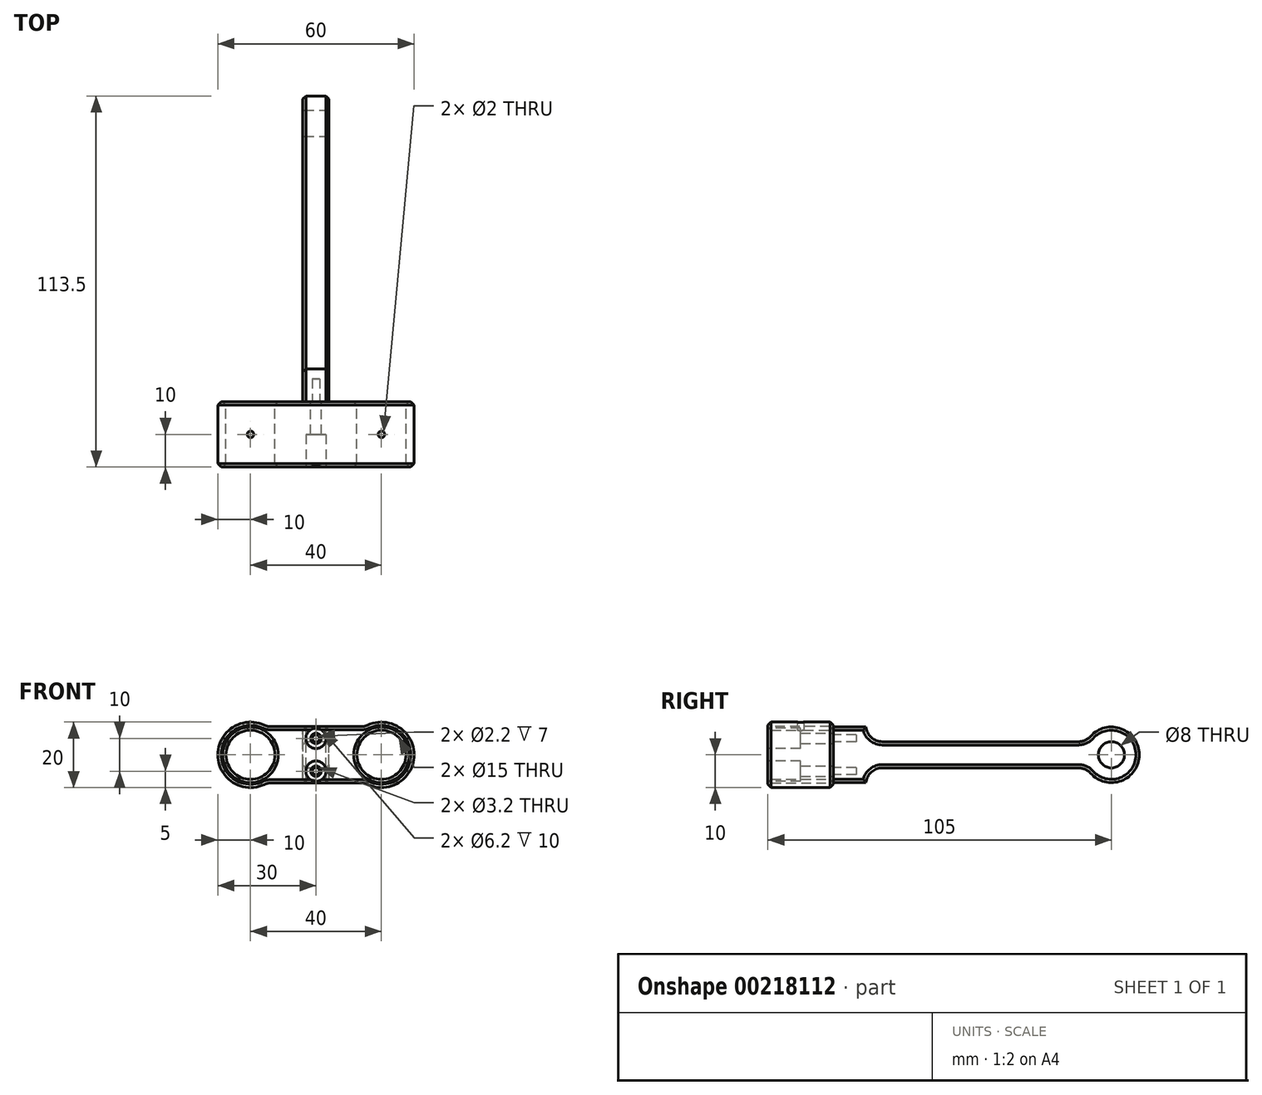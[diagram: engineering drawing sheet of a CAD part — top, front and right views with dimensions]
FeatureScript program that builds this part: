
annotation { "Feature Type Name" : "Feature", "Feature Type Description" : "" }
export const myFeature = defineFeature(function(context is Context, id is Id, definition is map)
    precondition{}
    {
        {
            var Q0;
            Q0=qCreatedBy(makeId("Front.planeOp"),FACE);
            var sketch = newSketch(context, id + "F0", { "sketchPlane" : qUnion([Q0])});
            skPoint(sketch, "E0.middle", {"position": v(0, 0) * mm});
            skCircle(sketch, "E1", {"center": v(-20, 0) * mm, "radius": 7.5 * mm});
            skCircle(sketch, "E2", {"center": v(20, 0) * mm, "radius": 7.5 * mm});
            skCircle(sketch, "E3", {"center": v(0, 5) * mm, "radius": 1.6 * mm});
            skCircle(sketch, "E4", {"center": v(0, -5) * mm, "radius": 1.6 * mm});
            skArc(sketch, "E5", {"start": v(-14.89, 8.6) * mm, "mid": v(-30, 0) * mm, "end": v(-14.89, -8.6) * mm});
            skArc(sketch, "E6", {"start": v(14.89, -8.6) * mm, "mid": v(30, 0) * mm, "end": v(14.89, 8.6) * mm});
            skLineSegment(sketch, "E7.bottom", {"start": v(14.89, 8.6) * mm, "end": v(-14.89, 8.6) * mm});
            skLineSegment(sketch, "E7.top", {"start": v(14.89, -8.6) * mm, "end": v(-14.89, -8.6) * mm});
            skPoint(sketch, "E8.orphan", {"position": v(30, 10) * mm});
            skPoint(sketch, "E9.orphan", {"position": v(-30, 10) * mm});
            skPoint(sketch, "E10.orphan", {"position": v(-30, -10) * mm});
            skPoint(sketch, "E0.left.start.orphan", {"position": v(30, -10) * mm});
            skSolve(sketch);
        }
        {
            var Q0;
            Q0=makeQuery(id+"F0.imprint","IMPRINT",FACE,{"disambiguationData":[TD([[makeQuery(id+"F0.imprint","IMPRINT",EDGE,{"derivedFrom":sQuery(id+"F0.wireOp",EDGE,"E0.bottom")}),-1.0]])]});
            var Q1;
            Q1=makeQuery(id+"F0.imprint","IMPRINT",FACE,{"disambiguationData":[TD([[makeQuery(id+"F0.imprint","IMPRINT",EDGE,{"derivedFrom":sQuery(id+"F0.wireOp",EDGE,"E1")}),-1.0]])]});
            extrude(context, id + "F1", {"entities" : qUnion([Q0, Q1]), "depth" : 20 * mm});
        }
        {
            var Q0;
            Q0=makeQuery(id+"F1.opExtrude","CAP_FACE",FACE,{"disambiguationData":[OSD([sQuery(id+"F0.wireOp",EDGE,"E0.bottom"),sQuery(id+"F0.wireOp",EDGE,"E0.top"),sQuery(id+"F0.wireOp",EDGE,"E0.left"),sQuery(id+"F0.wireOp",EDGE,"E0.right"),sQuery(id+"F0.wireOp",EDGE,"E1"),sQuery(id+"F0.wireOp",EDGE,"E2"),sQuery(id+"F0.wireOp",EDGE,"E3"),sQuery(id+"F0.wireOp",EDGE,"E4")])],"isStart":true});
            var sketch = newSketch(context, id + "F2", { "sketchPlane" : qUnion([Q0])});
            skLineSegment(sketch, "E11.bottom", {"start": v(4, -8.5) * mm, "end": v(-4, -8.5) * mm});
            skLineSegment(sketch, "E11.top", {"start": v(4, 8.5) * mm, "end": v(-4, 8.5) * mm});
            skLineSegment(sketch, "E11.left", {"start": v(4, -8.5) * mm, "end": v(4, 8.5) * mm});
            skLineSegment(sketch, "E11.right", {"start": v(-4, -8.5) * mm, "end": v(-4, 8.5) * mm});
            skPoint(sketch, "E11.middle", {"position": v(0, 0) * mm});
            skCircle(sketch, "E12", {"center": v(0, 5) * mm, "radius": 1.1 * mm});
            skCircle(sketch, "E13", {"center": v(0, -5) * mm, "radius": 1.1 * mm});
            skSolve(sketch);
        }
        {
            var Q0;
            Q0 = qSketchRegion(id + "F2", true);
            var Q1;
            Q1=makeQuery(id+"F2.imprint","IMPRINT",FACE,{"disambiguationData":[TD([[makeQuery(id+"F2.imprint","IMPRINT",EDGE,{"derivedFrom":sQuery(id+"F2.wireOp",EDGE,"E12")}),1.0]])]});
            var Q2;
            Q2=makeQuery(id+"F2.imprint","IMPRINT",FACE,{"disambiguationData":[TD([[makeQuery(id+"F2.imprint","IMPRINT",EDGE,{"derivedFrom":sQuery(id+"F2.wireOp",EDGE,"E13")}),1.0]])]});
            extrude(context, id + "F3", {"entities" : qUnion([Q0, Q1, Q2]), "depth" : 95 * mm});
        }
        {
            var Q0;
            Q0=makeQuery(id+"F2.imprint","IMPRINT",FACE,{"disambiguationData":[TD([[makeQuery(id+"F2.imprint","IMPRINT",EDGE,{"derivedFrom":sQuery(id+"F2.wireOp",EDGE,"E12")}),1.0]])]});
            var Q1;
            Q1=makeQuery(id+"F2.imprint","IMPRINT",FACE,{"disambiguationData":[TD([[makeQuery(id+"F2.imprint","IMPRINT",EDGE,{"derivedFrom":sQuery(id+"F2.wireOp",EDGE,"E13")}),1.0]])]});
            extrude(context, id + "F4", {"entities" : qUnion([Q0, Q1]), "operationType" : NewBodyOperationType.REMOVE, "depth" : 7 * mm});
        }
        {
            var Q0;
            Q0=makeQuery(id+"F1.opExtrude","CAP_FACE",FACE,{"disambiguationData":[OSD([sQuery(id+"F0.wireOp",EDGE,"E0.bottom"),sQuery(id+"F0.wireOp",EDGE,"E0.top"),sQuery(id+"F0.wireOp",EDGE,"E0.left"),sQuery(id+"F0.wireOp",EDGE,"E0.right"),sQuery(id+"F0.wireOp",EDGE,"E1"),sQuery(id+"F0.wireOp",EDGE,"E2"),sQuery(id+"F0.wireOp",EDGE,"E3"),sQuery(id+"F0.wireOp",EDGE,"E4")])],"isStart":false});
            var sketch = newSketch(context, id + "F5", { "sketchPlane" : qUnion([Q0])});
            skCircle(sketch, "E14", {"center": v(0, 5) * mm, "radius": 3.1 * mm});
            skCircle(sketch, "E15", {"center": v(0, -5) * mm, "radius": 3.1 * mm});
            skSolve(sketch);
        }
        {
            var Q0;
            Q0=makeQuery(id+"F5.imprint","IMPRINT",FACE,{"disambiguationData":[TD([[makeQuery(id+"F5.imprint","IMPRINT",EDGE,{"derivedFrom":sQuery(id+"F5.wireOp",EDGE,"E14")}),1.0]])]});
            var Q1;
            Q1=makeQuery(id+"F5.imprint","IMPRINT",FACE,{"disambiguationData":[TD([[makeQuery(id+"F5.imprint","IMPRINT",EDGE,{"derivedFrom":sQuery(id+"F5.wireOp",EDGE,"E15")}),1.0]])]});
            extrude(context, id + "F6", {"entities" : qUnion([Q0, Q1]), "operationType" : NewBodyOperationType.REMOVE, "oppositeDirection" : true, "depth" : 10 * mm});
        }
        {
            var Q0;
            Q0=makeQuery(id+"F3.opExtrude","SWEPT_FACE",FACE,{"disambiguationData":[OSD([sQuery(id+"F2.wireOp",EDGE,"E11.left")])]});
            var sketch = newSketch(context, id + "F7", { "sketchPlane" : qUnion([Q0])});
            skCircle(sketch, "E16", {"center": v(-85, 0) * mm, "radius": 4 * mm});
            skSolve(sketch);
        }
        {
            var Q0;
            Q0=makeQuery(id+"F7.imprint","IMPRINT",FACE,{"disambiguationData":[TD([[makeQuery(id+"F7.imprint","IMPRINT",EDGE,{"derivedFrom":sQuery(id+"F7.wireOp",EDGE,"E16")}),1.0]])]});
            extrude(context, id + "F8", {"entities" : qUnion([Q0]), "operationType" : NewBodyOperationType.REMOVE, "oppositeDirection" : true, "depth" : 25 * mm});
        }
        {
            var Q0;
            Q0=makeQuery(id+"F3.opExtrude","SWEPT_FACE",FACE,{"disambiguationData":[OSD([sQuery(id+"F2.wireOp",EDGE,"E11.left")])]});
            var sketch = newSketch(context, id + "F9", { "sketchPlane" : qUnion([Q0])});
            skCircle(sketch, "E17", {"center": v(-85, 0) * mm, "radius": 8 * mm});
            skSolve(sketch);
        }
        {
            var Q0;
            Q0=makeQuery(id+"F3.opExtrude","SWEPT_FACE",FACE,{"disambiguationData":[OSD([sQuery(id+"F2.wireOp",EDGE,"E11.right")])]});
            var sketch = newSketch(context, id + "F10", { "sketchPlane" : qUnion([Q0])});
            skCircle(sketch, "E18", {"center": v(85, 0) * mm, "radius": 8 * mm});
            skSolve(sketch);
        }
        {
            var Q0;
            Q0=qCreatedBy(makeId("Top.planeOp"),FACE);
            var sketch = newSketch(context, id + "F11", { "sketchPlane" : qUnion([Q0])});
            skLineSegment(sketch, "E19", {"start": v(-32.02, -10) * mm, "end": v(37.35, -10) * mm});
            skCircle(sketch, "E20", {"center": v(-20, -10) * mm, "radius": 1 * mm});
            skCircle(sketch, "E21", {"center": v(20, -10) * mm, "radius": 1 * mm});
            skSolve(sketch);
        }
        {
            var Q0;
            Q0 = qSketchRegion(id + "F11", true);
            extrude(context, id + "F12", {"entities" : qUnion([Q0]), "operationType" : NewBodyOperationType.REMOVE, "depth" : 15 * mm});
        }
        {
            var Q0;
            Q0=qCreatedBy(makeId("Right.planeOp"),FACE);
            var sketch = newSketch(context, id + "F13", { "sketchPlane" : qUnion([Q0])});
            skArc(sketch, "E22", {"start": v(77.5, -4) * mm, "mid": v(93.5, 0) * mm, "end": v(77.5, 4) * mm});
            skLineSegment(sketch, "E23.bottom", {"start": v(0, 10) * mm, "end": v(10, 10) * mm});
            skLineSegment(sketch, "E23.top", {"start": v(0, -10) * mm, "end": v(10, -10) * mm});
            skLineSegment(sketch, "E23.right", {"start": v(10, 10) * mm, "end": v(10, 4) * mm});
            skLineSegment(sketch, "E24.bottom", {"start": v(77.5, -4) * mm, "end": v(10, -4) * mm});
            skLineSegment(sketch, "E24.top", {"start": v(77.5, 4) * mm, "end": v(10, 4) * mm});
            skPoint(sketch, "E24.middle", {"position": v(40.86, 0) * mm});
            skPoint(sketch, "E25.orphan", {"position": v(78.2, -4) * mm});
            skPoint(sketch, "E26.orphan", {"position": v(78.52, 4) * mm});
            skPoint(sketch, "E24.right.end.orphan", {"position": v(3.52, 4) * mm});
            skPoint(sketch, "E27.orphan", {"position": v(3.2, -4) * mm});
            skLineSegment(sketch, "E28.trimOffspring", {"start": v(10, -4) * mm, "end": v(10, -10) * mm});
            skLineSegment(sketch, "E29", {"start": v(0, 10) * mm, "end": v(0, 24.73) * mm});
            skLineSegment(sketch, "E30", {"start": v(0, 24.73) * mm, "end": v(98.25, 24.73) * mm});
            skLineSegment(sketch, "E31", {"start": v(98.25, 24.73) * mm, "end": v(98.25, -15.35) * mm});
            skLineSegment(sketch, "E32", {"start": v(98.25, -15.35) * mm, "end": v(0, -17.47) * mm});
            skLineSegment(sketch, "E33", {"start": v(0, -17.47) * mm, "end": v(0, -10) * mm});
            skSolve(sketch);
        }
        {
            var Q0;
            Q0=makeQuery(id+"F1.opExtrude","SWEPT_EDGE",EDGE,{"disambiguationData":[OSD([sQuery(id+"F0.wireOp",EDGE,"E5"),sQuery(id+"F0.wireOp",EDGE,"E7.bottom")])]});
            fillet(context, id + "F14", {"entities" : qUnion([Q0]), "radius" : 5 * mm, "tangentPropagation" : true, "allowEdgeOverflow" : false});
        }
        {
            var Q0;
            Q0=makeQuery(id+"F1.opExtrude","SWEPT_EDGE",EDGE,{"disambiguationData":[OSD([sQuery(id+"F0.wireOp",EDGE,"E5"),sQuery(id+"F0.wireOp",EDGE,"E7.top")])]});
            var Q1;
            Q1=makeQuery(id+"F1.opExtrude","SWEPT_EDGE",EDGE,{"disambiguationData":[OSD([sQuery(id+"F0.wireOp",EDGE,"E6"),sQuery(id+"F0.wireOp",EDGE,"E7.top")])]});
            var Q2;
            Q2=makeQuery(id+"F1.opExtrude","SWEPT_EDGE",EDGE,{"disambiguationData":[OSD([sQuery(id+"F0.wireOp",EDGE,"E6"),sQuery(id+"F0.wireOp",EDGE,"E7.bottom")])]});
            fillet(context, id + "F15", {"entities" : qUnion([Q0, Q1, Q2]), "radius" : 5 * mm, "tangentPropagation" : true, "allowEdgeOverflow" : false});
        }
        {
            var Q0;
            Q0=makeQuery(id+"F13.imprint","IMPRINT",FACE,{"disambiguationData":[TD([[makeQuery(id+"F13.imprint","IMPRINT",EDGE,{"derivedFrom":sQuery(id+"F13.wireOp",EDGE,"E22")}),-1.0]])]});
            extrude(context, id + "F16", {"entities" : qUnion([Q0]), "operationType" : NewBodyOperationType.REMOVE, "endBound" : BoundingType.SYMMETRIC, "oppositeDirection" : true, "depth" : 25 * mm});
        }
        {
            var Q0;
            Q0=makeQuery(id+"F16.boolean.opBoolean","COPY",EDGE,{"derivedFrom":makeQuery(id+"F16.opExtrude","SWEPT_EDGE",EDGE,{"disambiguationData":[OSD([sQuery(id+"F13.wireOp",EDGE,"E23.right"),sQuery(id+"F13.wireOp",EDGE,"E24.top")])]})});
            var Q1;
            Q1=makeQuery(id+"F16.boolean.opBoolean","COPY",EDGE,{"derivedFrom":makeQuery(id+"F16.opExtrude","SWEPT_EDGE",EDGE,{"disambiguationData":[OSD([sQuery(id+"F13.wireOp",EDGE,"E24.bottom"),sQuery(id+"F13.wireOp",EDGE,"E28.trimOffspring")])]})});
            fillet(context, id + "F17", {"entities" : qUnion([Q0, Q1]), "radius" : 5 * mm, "tangentPropagation" : true, "allowEdgeOverflow" : false});
        }
        {
            var Q0;
            Q0=makeQuery(id+"F16.boolean.opBoolean","COPY",EDGE,{"derivedFrom":makeQuery(id+"F16.opExtrude","SWEPT_EDGE",EDGE,{"disambiguationData":[OSD([sQuery(id+"F13.wireOp",EDGE,"E22"),sQuery(id+"F13.wireOp",EDGE,"E24.top")])]})});
            var Q1;
            Q1=makeQuery(id+"F16.boolean.opBoolean","COPY",EDGE,{"derivedFrom":makeQuery(id+"F16.opExtrude","SWEPT_EDGE",EDGE,{"disambiguationData":[OSD([sQuery(id+"F13.wireOp",EDGE,"E22"),sQuery(id+"F13.wireOp",EDGE,"E24.bottom")])]})});
            fillet(context, id + "F18", {"entities" : qUnion([Q0, Q1]), "radius" : 5 * mm, "tangentPropagation" : true, "allowEdgeOverflow" : false});
        }
        {
            var Q0;
            Q0=makeQuery(id+"F1.opExtrude","CAP_EDGE",EDGE,{"disambiguationData":[OSD([sQuery(id+"F0.wireOp",EDGE,"E1")])],"isStart":true});
            var Q1;
            Q1=makeQuery(id+"F1.opExtrude","CAP_EDGE",EDGE,{"disambiguationData":[OSD([sQuery(id+"F0.wireOp",EDGE,"E2")])],"isStart":true});
            var Q2;
            Q2=makeQuery(id+"F1.opExtrude","CAP_EDGE",EDGE,{"disambiguationData":[OSD([sQuery(id+"F0.wireOp",EDGE,"E7.top")])],"isStart":true});
            var Q3;
            Q3=makeQuery(id+"F1.opExtrude","CAP_EDGE",EDGE,{"disambiguationData":[OSD([sQuery(id+"F0.wireOp",EDGE,"E7.top")])],"isStart":false});
            var Q4;
            Q4=makeQuery(id+"F1.opExtrude","CAP_EDGE",EDGE,{"disambiguationData":[OSD([sQuery(id+"F0.wireOp",EDGE,"E1")])],"isStart":false});
            var Q5;
            Q5=makeQuery(id+"F1.opExtrude","CAP_EDGE",EDGE,{"disambiguationData":[OSD([sQuery(id+"F0.wireOp",EDGE,"E2")])],"isStart":false});
            chamfer(context, id + "F19", {"entities" : qUnion([Q0, Q1, Q2, Q3, Q4, Q5]), "width" : 1 * mm, "tangentPropagation" : true});
        }
        {
            var Q0;
            Q0=makeQuery(id+"F16.boolean.opBoolean","INTERSECT",EDGE,{"derivedFrom":[makeQuery(id+"F3.opExtrude","SWEPT_FACE",FACE,{"disambiguationData":[OSD([sQuery(id+"F2.wireOp",EDGE,"E11.right")])]}),makeQuery(id+"F16.opExtrude","SWEPT_FACE",FACE,{"disambiguationData":[OSD([sQuery(id+"F13.wireOp",EDGE,"E24.bottom")])]})]});
            var Q1;
            Q1=makeQuery(id+"F16.boolean.opBoolean","INTERSECT",EDGE,{"derivedFrom":[makeQuery(id+"F3.opExtrude","SWEPT_FACE",FACE,{"disambiguationData":[OSD([sQuery(id+"F2.wireOp",EDGE,"E11.left")])]}),makeQuery(id+"F16.opExtrude","SWEPT_FACE",FACE,{"disambiguationData":[OSD([sQuery(id+"F13.wireOp",EDGE,"E24.bottom")])]})]});
            var Q2;
            Q2=makeQuery(id+"F3.opExtrude","SWEPT_EDGE",EDGE,{"disambiguationData":[OSD([sQuery(id+"F2.wireOp",EDGE,"E11.bottom"),sQuery(id+"F2.wireOp",EDGE,"E11.right")])]});
            var Q3;
            Q3=makeQuery(id+"F3.opExtrude","SWEPT_EDGE",EDGE,{"disambiguationData":[OSD([sQuery(id+"F2.wireOp",EDGE,"E11.top"),sQuery(id+"F2.wireOp",EDGE,"E11.right")])]});
            var Q4;
            Q4=makeQuery(id+"F3.opExtrude","SWEPT_EDGE",EDGE,{"disambiguationData":[OSD([sQuery(id+"F2.wireOp",EDGE,"E11.bottom"),sQuery(id+"F2.wireOp",EDGE,"E11.left")])]});
            var Q5;
            Q5=makeQuery(id+"F3.opExtrude","SWEPT_EDGE",EDGE,{"disambiguationData":[OSD([sQuery(id+"F2.wireOp",EDGE,"E11.top"),sQuery(id+"F2.wireOp",EDGE,"E11.left")])]});
            chamfer(context, id + "F20", {"entities" : qUnion([Q0, Q1, Q2, Q3, Q4, Q5]), "width" : 1 * mm, "tangentPropagation" : true});
        }
    });
